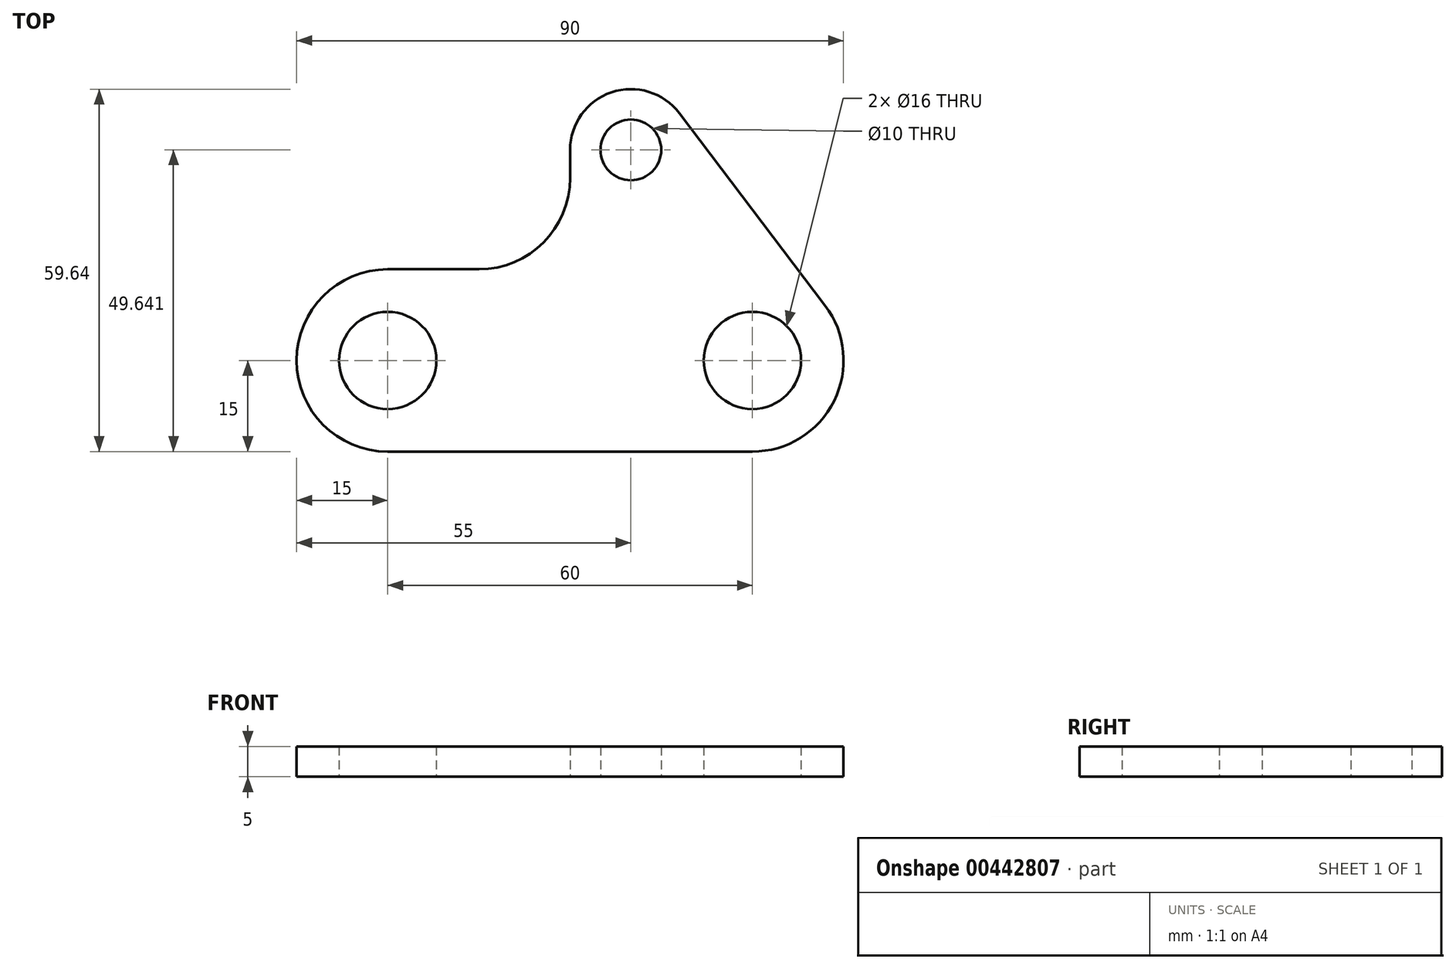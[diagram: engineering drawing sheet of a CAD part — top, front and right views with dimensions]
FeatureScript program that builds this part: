
annotation { "Feature Type Name" : "Feature", "Feature Type Description" : "" }
export const myFeature = defineFeature(function(context is Context, id is Id, definition is map)
    precondition{}
    {
        {
            var Q0;
            Q0=qCreatedBy(makeId("Top.planeOp"),FACE);
            var sketch = newSketch(context, id + "F0", { "sketchPlane" : qUnion([Q0])});
            skArc(sketch, "E0", {"start": v(0, 15) * mm, "mid": v(-15, 0) * mm, "end": v(0, -15) * mm});
            skArc(sketch, "E1", {"start": v(60, -15) * mm, "mid": v(73.43, -6.67) * mm, "end": v(71.95, 9.06) * mm});
            skArc(sketch, "E2", {"start": v(47.97, 40.68) * mm, "mid": v(36.81, 44.12) * mm, "end": v(30, 34.64) * mm});
            skArc(sketch, "E3", {"start": v(15, 15) * mm, "mid": v(25.6, 19.4) * mm, "end": v(30, 30) * mm});
            skLineSegment(sketch, "E4", {"start": v(0, -15) * mm, "end": v(60, -15) * mm});
            skLineSegment(sketch, "E5", {"start": v(71.95, 9.06) * mm, "end": v(47.97, 40.68) * mm});
            skLineSegment(sketch, "E6", {"start": v(30, 34.64) * mm, "end": v(30, 30) * mm});
            skLineSegment(sketch, "E7", {"start": v(15, 15) * mm, "end": v(-21.46, 15) * mm});
            skCircle(sketch, "E8", {"center": v(0, 0) * mm, "radius": 8 * mm});
            skCircle(sketch, "E9", {"center": v(60, 0) * mm, "radius": 8 * mm});
            skCircle(sketch, "E10", {"center": v(40, 34.64) * mm, "radius": 5 * mm});
            skSolve(sketch);
        }
        {
            var Q0;
            {var subQ1=sQuery(id+"F0.wireOp",EDGE,"E0");Q0=makeQuery(id+"F0.imprint","IMPRINT",FACE,{"disambiguationData":[TD([[makeQuery(id+"F0.imprint","IMPRINT",EDGE,{"derivedFrom":subQ1}),1.0]])]});}
            extrude(context, id + "F1", {"entities" : qUnion([Q0]), "depth" : 5 * mm});
        }
    });
